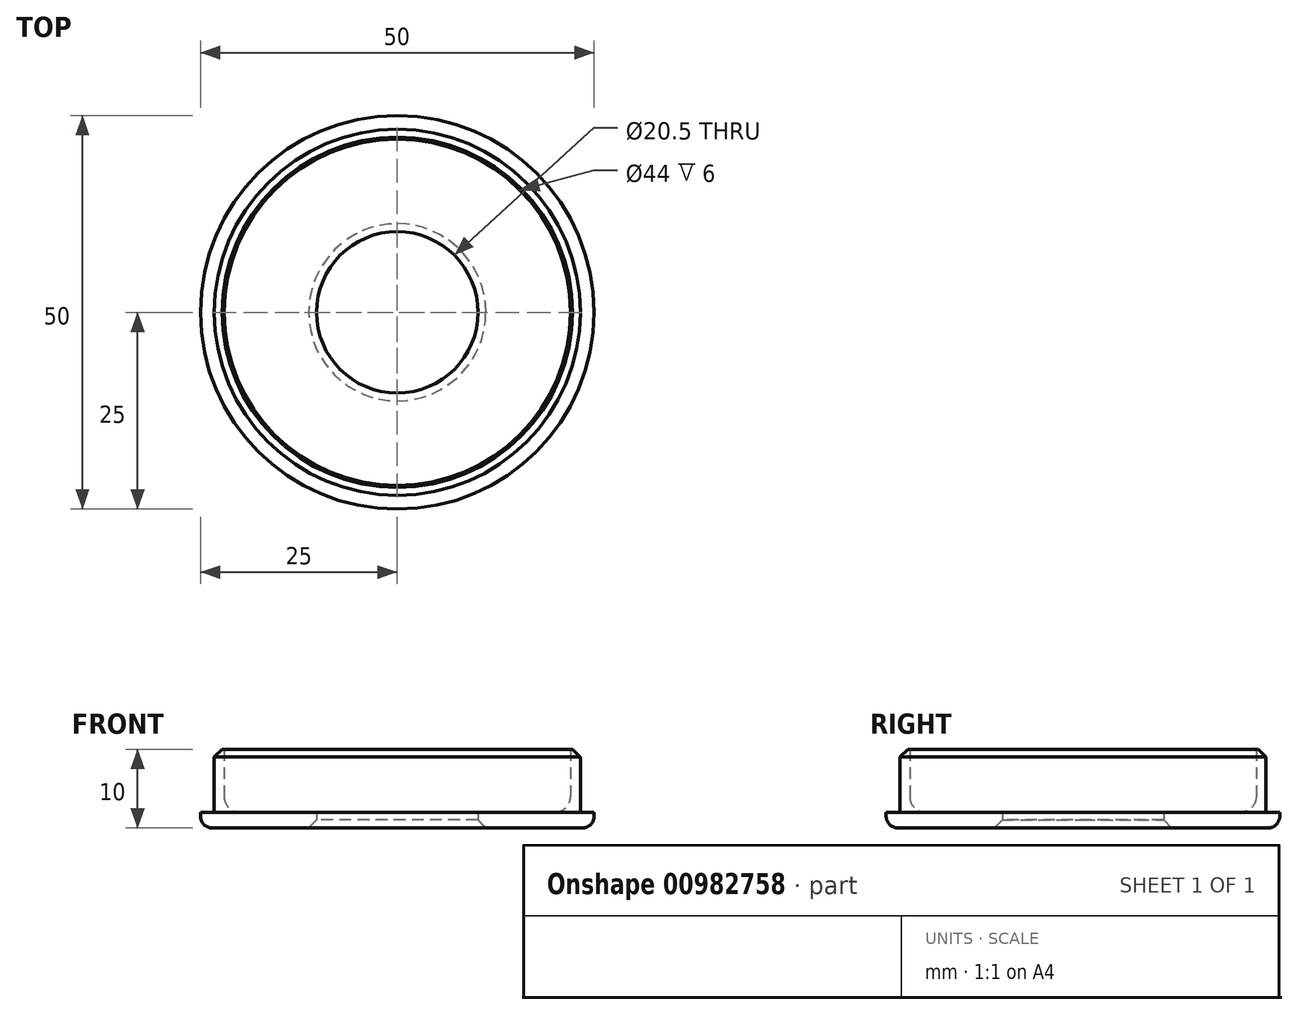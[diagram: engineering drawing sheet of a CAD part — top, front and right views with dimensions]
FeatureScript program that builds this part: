
annotation { "Feature Type Name" : "Feature", "Feature Type Description" : "" }
export const myFeature = defineFeature(function(context is Context, id is Id, definition is map)
    precondition{}
    {
        {
            var Q0;
            Q0=qCreatedBy(makeId("Top.planeOp"),FACE);
            var sketch = newSketch(context, id + "F0", { "sketchPlane" : qUnion([Q0])});
            skCircle(sketch, "E0", {"center": v(0, 0) * mm, "radius": 25 * mm});
            skCircle(sketch, "E1", {"center": v(0, 0) * mm, "radius": 10.25 * mm});
            skSolve(sketch);
        }
        {
            var Q0;
            Q0=makeQuery(id+"F0.imprint","IMPRINT",FACE,{"disambiguationData":[TD([[makeQuery(id+"F0.imprint","IMPRINT",EDGE,{"derivedFrom":sQuery(id+"F0.wireOp",EDGE,"E0")}),1.0]])]});
            extrude(context, id + "F1", {"entities" : qUnion([Q0]), "depth" : 2 * mm, "offsetDistance" : 25 * mm});
        }
        {
            var Q0;
            Q0=makeQuery(id+"F1.opExtrude","CAP_FACE",FACE,{"disambiguationData":[OSD([sQuery(id+"F0.wireOp",EDGE,"E0"),sQuery(id+"F0.wireOp",EDGE,"E1")])],"isStart":false});
            var sketch = newSketch(context, id + "F2", { "sketchPlane" : qUnion([Q0])});
            skCircle(sketch, "E2", {"center": v(0, 0) * mm, "radius": 23.25 * mm});
            skCircle(sketch, "E3", {"center": v(0, 0) * mm, "radius": 22 * mm});
            skSolve(sketch);
        }
        {
            var Q0;
            Q0=makeQuery(id+"F2.imprint","IMPRINT",FACE,{"disambiguationData":[TD([[makeQuery(id+"F2.imprint","IMPRINT",EDGE,{"derivedFrom":sQuery(id+"F2.wireOp",EDGE,"E2")}),1.0]])]});
            extrude(context, id + "F3", {"entities" : qUnion([Q0]), "operationType" : NewBodyOperationType.ADD, "depth" : 8 * mm, "offsetDistance" : 25 * mm});
        }
        {
            var Q0;
            Q0=makeQuery(id+"F3.opExtrude","CAP_EDGE",EDGE,{"disambiguationData":[OSD([sQuery(id+"F2.wireOp",EDGE,"E2")])],"isStart":false});
            chamfer(context, id + "F4", {"entities" : qUnion([Q0]), "width" : 1 * mm, "tangentPropagation" : true});
        }
        {
            var Q0;
            Q0=makeQuery(id+"F1.opExtrude","CAP_EDGE",EDGE,{"disambiguationData":[OSD([sQuery(id+"F0.wireOp",EDGE,"E0")])],"isStart":true});
            fillet(context, id + "F5", {"entities" : qUnion([Q0]), "radius" : 1.5 * mm, "tangentPropagation" : true, "allowEdgeOverflow" : false});
        }
        {
            var Q0;
            Q0=makeQuery(id+"F1.opExtrude","CAP_EDGE",EDGE,{"disambiguationData":[OSD([sQuery(id+"F0.wireOp",EDGE,"E1")])],"isStart":true});
            chamfer(context, id + "F6", {"entities" : qUnion([Q0]), "width" : 1 * mm, "tangentPropagation" : true});
        }
        {
            var Q0;
            Q0=makeQuery(id+"F3.opExtrude","CAP_EDGE",EDGE,{"disambiguationData":[OSD([sQuery(id+"F2.wireOp",EDGE,"E3")])],"isStart":true});
            fillet(context, id + "F7", {"entities" : qUnion([Q0]), "radius" : 2 * mm, "tangentPropagation" : true, "allowEdgeOverflow" : false});
        }
    });
